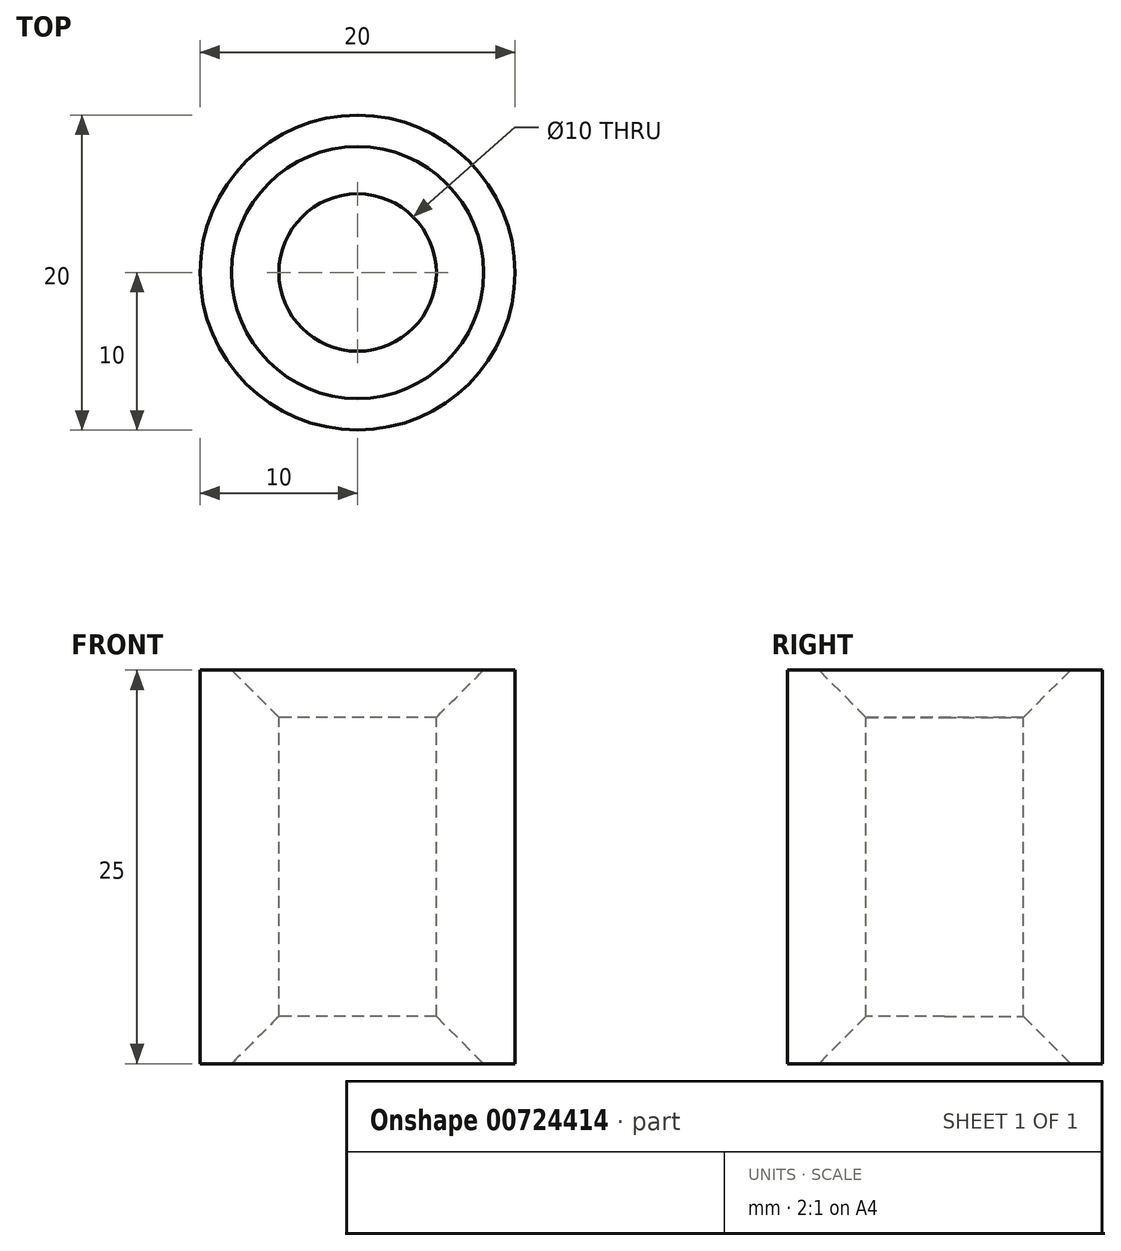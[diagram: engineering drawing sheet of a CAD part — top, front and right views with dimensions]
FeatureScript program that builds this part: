
annotation { "Feature Type Name" : "Feature", "Feature Type Description" : "" }
export const myFeature = defineFeature(function(context is Context, id is Id, definition is map)
    precondition{}
    {
        {
            var Q0;
            Q0=qCreatedBy(makeId("Top.planeOp"),FACE);
            var sketch = newSketch(context, id + "F0", { "sketchPlane" : qUnion([Q0])});
            skCircle(sketch, "E0", {"center": v(0, 0) * mm, "radius": 10 * mm});
            skSolve(sketch);
        }
        {
            var Q0;
            Q0=makeQuery(id+"F0.imprint","IMPRINT",FACE,{"disambiguationData":[TD([[makeQuery(id+"F0.imprint","IMPRINT",EDGE,{"derivedFrom":sQuery(id+"F0.wireOp",EDGE,"E0")}),1.0]])]});
            extrude(context, id + "F1", {"entities" : qUnion([Q0]), "depth" : 25 * mm, "offsetDistance" : 25 * mm});
        }
        {
            var Q0;
            Q0=makeQuery(id+"F1.opExtrude","CAP_FACE",FACE,{"disambiguationData":[OSD([sQuery(id+"F0.wireOp",EDGE,"E0")])],"isStart":false});
            var sketch = newSketch(context, id + "F2", { "sketchPlane" : qUnion([Q0])});
            skCircle(sketch, "E1", {"center": v(0, 0) * mm, "radius": 6 * mm});
            skSolve(sketch);
        }
        {
            var Q0;
            Q0=sQuery(id+"F2.wireOp",VERTEX,"E1.center");
            var Q1;
            Q1=makeQuery(id+"F1.opExtrude","SWEPT_BODY",BODY,{"disambiguationData":[OSD([sQuery(id+"F0.wireOp",EDGE,"E0")])]});
            hole(context, id + "F3", {"style" : HoleStyle.C_SINK, "endStyle" : HoleEndStyle.BLIND, "holeDiameter" : 10 * mm, "cSinkDiameter" : 16 * mm, "cSinkAngle" : 90 * degree, "majorDiameter" : 5 * mm, "holeDepth" : 15 * mm, "isTappedThrough" : true, "tappedDepth" : 12 * mm, "tapClearance" : 3, "startFromSketch" : true, "locations" : qUnion([Q0]), "scope" : qUnion([Q1])});
        }
        {
            var Q0;
            Q0=makeQuery(id+"F1.opExtrude","CAP_FACE",FACE,{"disambiguationData":[OSD([sQuery(id+"F0.wireOp",EDGE,"E0")])],"isStart":true});
            var sketch = newSketch(context, id + "F4", { "sketchPlane" : qUnion([Q0])});
            skCircle(sketch, "E2", {"center": v(0, 0) * mm, "radius": 5 * mm});
            skSolve(sketch);
        }
        {
            var Q0;
            Q0=sQuery(id+"F4.wireOp",VERTEX,"E2.center");
            var Q1;
            Q1=makeQuery(id+"F1.opExtrude","SWEPT_BODY",BODY,{"disambiguationData":[OSD([sQuery(id+"F0.wireOp",EDGE,"E0")])]});
            hole(context, id + "F5", {"style" : HoleStyle.C_SINK, "endStyle" : HoleEndStyle.BLIND, "holeDiameter" : 10 * mm, "cSinkDiameter" : 16 * mm, "cSinkAngle" : 90 * degree, "majorDiameter" : 5 * mm, "holeDepth" : 15 * mm, "isTappedThrough" : true, "tappedDepth" : 12 * mm, "tapClearance" : 3, "startFromSketch" : true, "locations" : qUnion([Q0]), "scope" : qUnion([Q1])});
        }
    });
